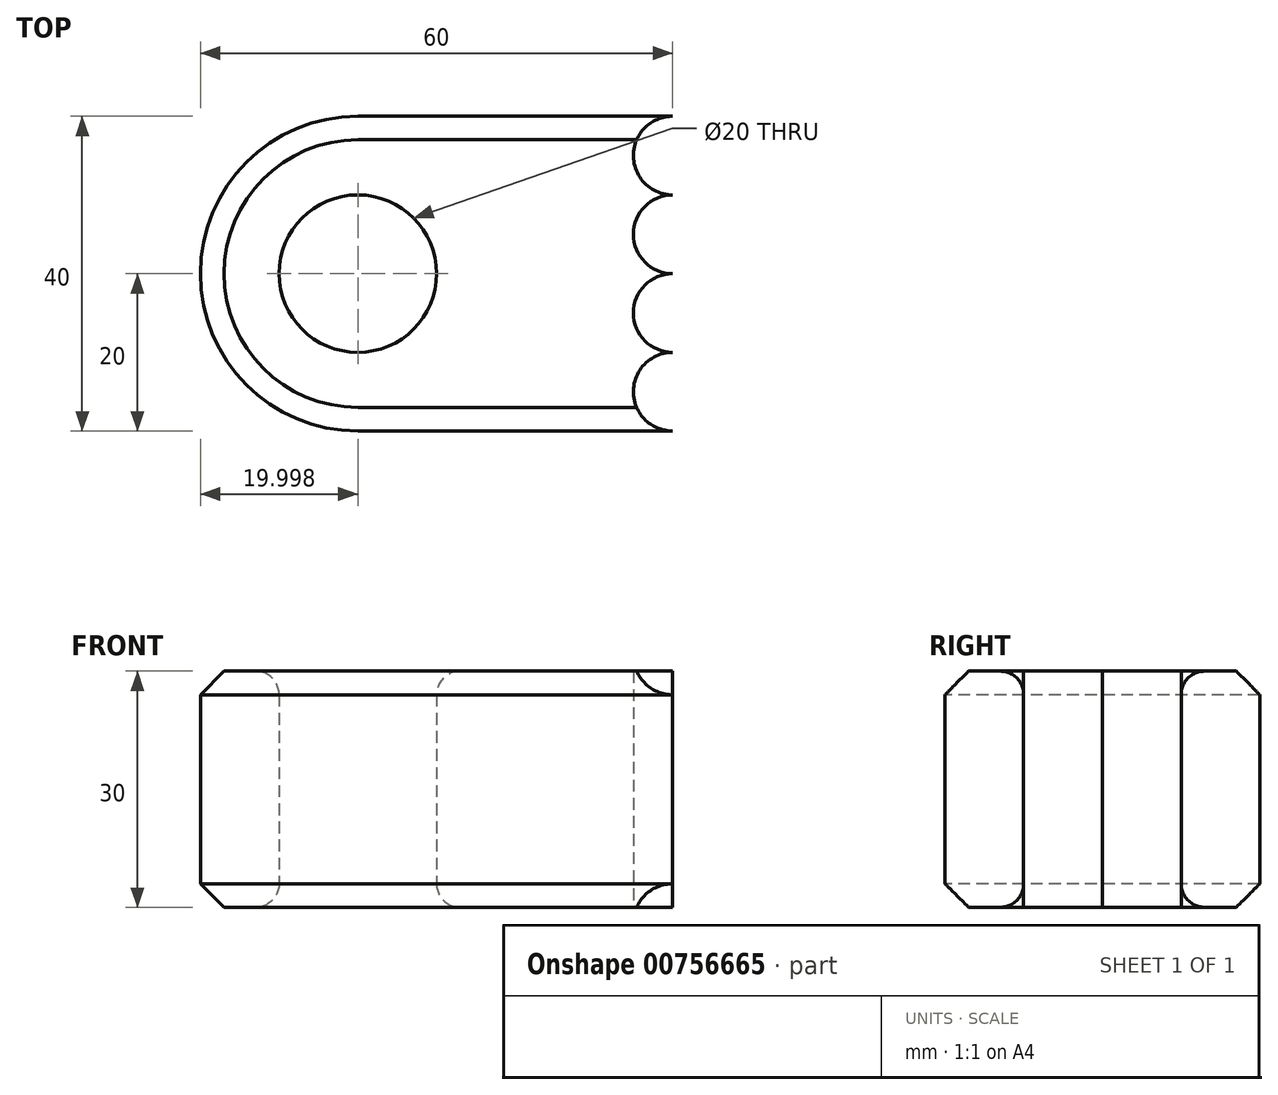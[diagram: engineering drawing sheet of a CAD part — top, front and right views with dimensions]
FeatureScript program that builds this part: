
annotation { "Feature Type Name" : "Feature", "Feature Type Description" : "" }
export const myFeature = defineFeature(function(context is Context, id is Id, definition is map)
    precondition{}
    {
        {
            var Q0;
            Q0=qCreatedBy(makeId("Top.planeOp"),FACE);
            var sketch = newSketch(context, id + "F0", { "sketchPlane" : qUnion([Q0])});
            skLineSegment(sketch, "E0.bottom", {"start": v(-19.44, 20) * mm, "end": v(20.56, 20) * mm});
            skLineSegment(sketch, "E0.top", {"start": v(-19.44, -20) * mm, "end": v(20.56, -20) * mm});
            skArc(sketch, "E1", {"start": v(-19.44, 20) * mm, "mid": v(-39.44, 0) * mm, "end": v(-19.44, -20) * mm});
            skCircle(sketch, "E2.0", {"center": v(-19.44, 0) * mm, "radius": 10 * mm});
            skArc(sketch, "E3", {"start": v(20.56, 20) * mm, "mid": v(15.56, 15) * mm, "end": v(20.56, 10) * mm});
            skArc(sketch, "E4", {"start": v(20.56, -10) * mm, "mid": v(15.56, -15) * mm, "end": v(20.56, -20) * mm});
            skArc(sketch, "E5", {"start": v(20.56, 0) * mm, "mid": v(15.56, -5) * mm, "end": v(20.56, -10) * mm});
            skArc(sketch, "E6", {"start": v(20.56, 10) * mm, "mid": v(15.56, 5) * mm, "end": v(20.56, 0) * mm});
            skPoint(sketch, "E7", {"position": v(-39.44, 0) * mm});
            skSolve(sketch);
        }
        {
            var Q0;
            Q0=makeQuery(id+"F0.imprint","IMPRINT",FACE,{"disambiguationData":[TD([[makeQuery(id+"F0.imprint","IMPRINT",EDGE,{"derivedFrom":sQuery(id+"F0.wireOp",EDGE,"E0.bottom")}),-1.0]])]});
            extrude(context, id + "F1", {"entities" : qUnion([Q0]), "endBound" : BoundingType.SYMMETRIC, "depth" : 30 * mm, "offsetDistance" : 25 * mm});
        }
        {
            var Q0;
            Q0=makeQuery(id+"F1.opExtrude","CAP_EDGE",EDGE,{"disambiguationData":[OSD([sQuery(id+"F0.wireOp",EDGE,"E2.0")])],"isStart":false});
            fillet(context, id + "F2", {"entities" : qUnion([Q0]), "radius" : 3 * mm, "tangentPropagation" : true, "allowEdgeOverflow" : false});
        }
        {
            var Q0;
            Q0=makeQuery(id+"F1.opExtrude","CAP_EDGE",EDGE,{"disambiguationData":[OSD([sQuery(id+"F0.wireOp",EDGE,"E2.0")])],"isStart":true});
            fillet(context, id + "F3", {"entities" : qUnion([Q0]), "radius" : 3 * mm, "tangentPropagation" : true, "allowEdgeOverflow" : false});
        }
        {
            var Q0;
            Q0=makeQuery(id+"F1.opExtrude","CAP_EDGE",EDGE,{"disambiguationData":[OSD([sQuery(id+"F0.wireOp",EDGE,"E0.bottom")])],"isStart":false});
            var Q1;
            Q1=makeQuery(id+"F1.opExtrude","CAP_EDGE",EDGE,{"disambiguationData":[OSD([sQuery(id+"F0.wireOp",EDGE,"E1")])],"isStart":false});
            var Q2;
            Q2=makeQuery(id+"F1.opExtrude","CAP_EDGE",EDGE,{"disambiguationData":[OSD([sQuery(id+"F0.wireOp",EDGE,"E0.top")])],"isStart":false});
            chamfer(context, id + "F4", {"entities" : qUnion([Q0, Q1, Q2]), "width" : 3 * mm, "tangentPropagation" : true});
        }
        {
            var Q0;
            Q0=makeQuery(id+"F1.opExtrude","CAP_EDGE",EDGE,{"disambiguationData":[OSD([sQuery(id+"F0.wireOp",EDGE,"E0.top")])],"isStart":true});
            var Q1;
            Q1=makeQuery(id+"F1.opExtrude","CAP_EDGE",EDGE,{"disambiguationData":[OSD([sQuery(id+"F0.wireOp",EDGE,"E1")])],"isStart":true});
            var Q2;
            Q2=makeQuery(id+"F1.opExtrude","CAP_EDGE",EDGE,{"disambiguationData":[OSD([sQuery(id+"F0.wireOp",EDGE,"E0.bottom")])],"isStart":true});
            chamfer(context, id + "F5", {"entities" : qUnion([Q0, Q1, Q2]), "width" : 3 * mm, "tangentPropagation" : true});
        }
    });
